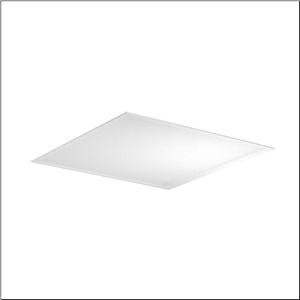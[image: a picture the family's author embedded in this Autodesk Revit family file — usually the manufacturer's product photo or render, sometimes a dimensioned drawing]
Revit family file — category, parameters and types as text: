
# Revit family: apollon_r__21_square_51mq12wd2t13_0a2d
name_source: partatom
category: Lighting Fixtures
units: mm (PartAtom-declared; Revit-internal decimal feet)

## family parameters
Cut with Voids When Loaded = No
Host = Face
Light Source = No
Part Type = Normal
Room Calculation Point = No
Round Connector Dimension = Use Diameter
Shared = No

## types (1)
- --- (1 x LED 2700 K ... 6500 K, 4000 lm, 40 W, 2700K)
    Apparent Load = 40 VA
    CIE Flux Codes = 61 87 97 100 100
    Color Rendering = 80
    Color Temperature = 2700K
    Default Elevation = 1800 mm
    Description = Apollon® 21 square, office luminaire, primary optical cover: micro prismatic cover, of PMMA, CAT 2 (L<= 3000cd/m²), light emission: direct distribution, primary light characteristic: symmetric, installation type: lay-in mounting, LED, rated luminous flux: 4.000lm, luminous efficacy: 100lm/W, light colour: 8tw, colour temperature: 2700..6500K, control gear: ECG DALI, with terminal, 5-pole, mains connection: 220..240V, AC, 50/60Hz, rated input power: 40W, housing, of aluminium, traffic white (RAL 9016), module: M600, length: 596mm, width: 596mm, height: 40mm, housing upper side, of sheet steel, galvanised, protection rating (complete): IP20, protection rating (lamp compartment, on room side): IP50, insulation class (complete): insulation class I (protective earthing), certification: CE, ENEC, permissible operating ambient temperature: -20..+40°C, packaging unit: 1 piece
    Height = 0 mm  [stored 0 ft]
    Lamp = 1 x LED 2700 K ... 6500 K
    Lamp Light Flux = 4000 lm
    Lamp Power = 40 W
    Lamp count = 1
    Length = 595 mm
    Luminous efficacy = 100 lm/W
    Manufacturer = Siteco
    ModVariant = No
    Model = 51MQ12WD2T13
    Mounting Place = Ceiling
    Mounting Type = Recessed
    Number of Poles = 1
    OnlyDefault = Yes
    Power Factor = 1
    Product Name = Apollon® 21 square
    Product group = office luminaire | ceiling recessed
    ProductGroupID = 401
    Protection Class = Protection class I
    Protection Degree = IP 20
    RLX_Detail_Level = 1
    RLX_Emergency_Light_Flux = 0 lm
    RLX_Emergency_Type = 0
    RLX_Emergency_Type_DB = No
    RlxData = <blob elided: 14701 chars, md5=4d273003>
    Socket = socket
    Standby Power = 0 W
    System Light Flux = 4000 lm
    System Power = 40 W
    Type Comments = individual setting: CCT=2700K
    Type Image = l_1291049.jpg
    URL = http://relux.com
    VarID = @adj_032443
    Voltage = 0 V
    Weight = 0.00 kg
    Width = 595 mm

note: [stored X ft] marks values corroborated as IEEE doubles in the binary element streams (Revit-internal decimal feet)

## geometry (parser evidence)
native form markers: Sweep x12
no freeform markers — native parametric forms only
